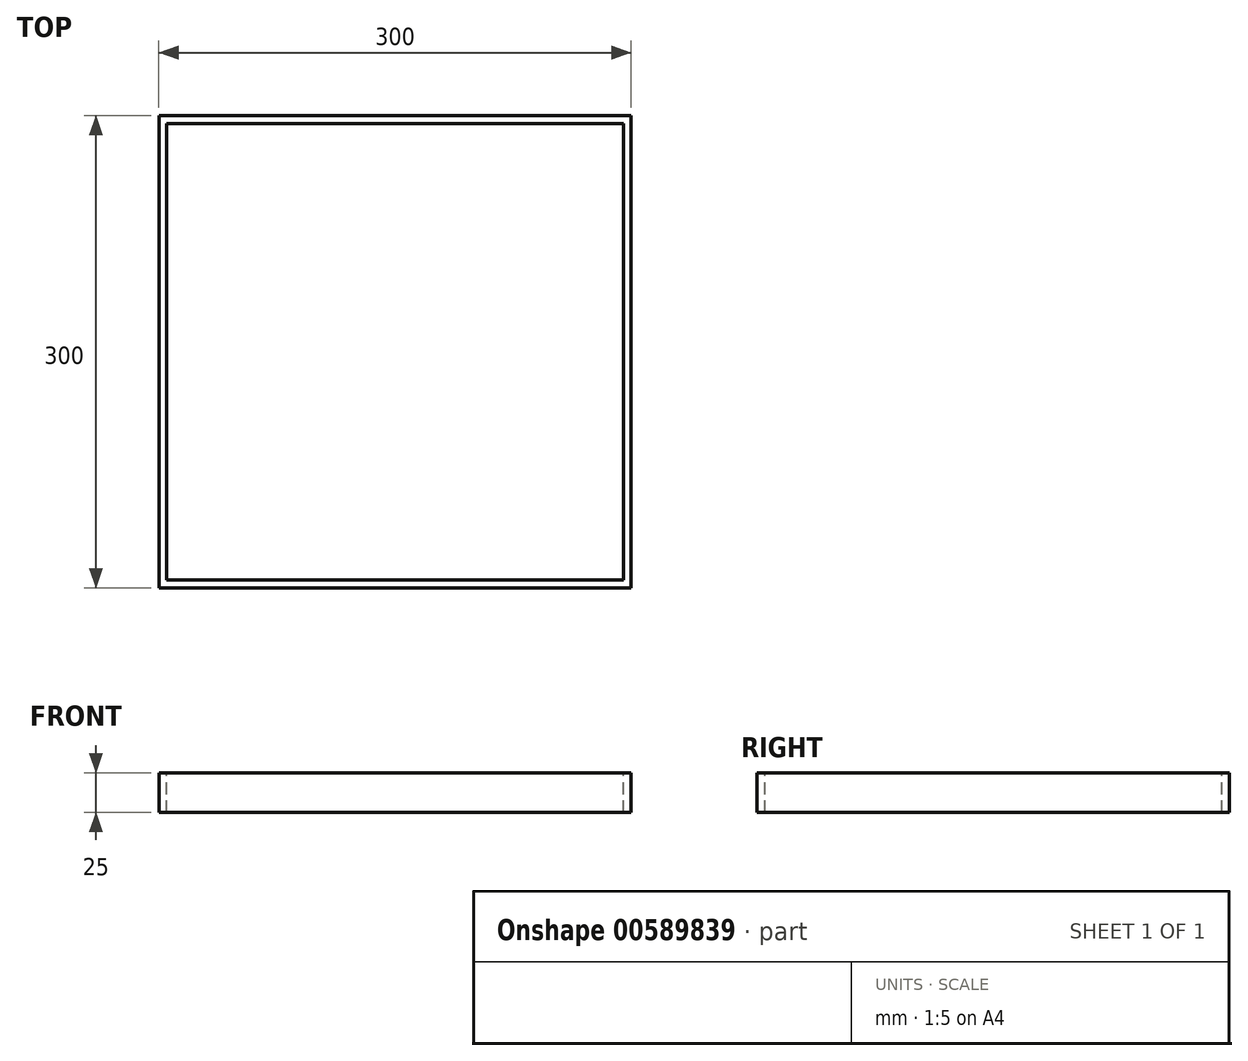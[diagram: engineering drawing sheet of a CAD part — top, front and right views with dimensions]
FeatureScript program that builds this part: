
annotation { "Feature Type Name" : "Feature", "Feature Type Description" : "" }
export const myFeature = defineFeature(function(context is Context, id is Id, definition is map)
    precondition{}
    {
        {
            var Q0;
            Q0=qCreatedBy(makeId("Top.planeOp"),FACE);
            var sketch = newSketch(context, id + "F0", { "sketchPlane" : qUnion([Q0])});
            skLineSegment(sketch, "E0.bottom", {"start": v(-140.23, 161.75) * mm, "end": v(159.77, 161.75) * mm});
            skLineSegment(sketch, "E0.top", {"start": v(-140.23, -138.25) * mm, "end": v(159.77, -138.25) * mm});
            skLineSegment(sketch, "E0.left", {"start": v(-140.23, 161.75) * mm, "end": v(-140.23, -138.25) * mm});
            skLineSegment(sketch, "E0.right", {"start": v(159.77, 161.75) * mm, "end": v(159.77, -138.25) * mm});
            skLineSegment(sketch, "E1.0", {"start": v(-135.23, 156.75) * mm, "end": v(154.77, 156.75) * mm});
            skLineSegment(sketch, "E2.0", {"start": v(-135.23, 156.75) * mm, "end": v(-135.23, -133.25) * mm});
            skLineSegment(sketch, "E3.0", {"start": v(-135.23, -133.25) * mm, "end": v(154.77, -133.25) * mm});
            skLineSegment(sketch, "E4.0", {"start": v(154.77, 156.75) * mm, "end": v(154.77, -133.25) * mm});
            skSolve(sketch);
        }
        {
            var Q0;
            Q0=sQuery(id+"F0.wireOp",EDGE,"E4.0");
            var Q1;
            Q1=sQuery(id+"F0.wireOp",EDGE,"E0.right");
            var Q2;
            Q2=sQuery(id+"F0.wireOp",EDGE,"E0.bottom");
            var Q3;
            Q3=sQuery(id+"F0.wireOp",EDGE,"E1.0");
            var Q4;
            Q4=sQuery(id+"F0.wireOp",EDGE,"E0.left");
            var Q5;
            Q5=sQuery(id+"F0.wireOp",EDGE,"E2.0");
            var Q6;
            Q6=sQuery(id+"F0.wireOp",EDGE,"E3.0");
            var Q7;
            Q7=sQuery(id+"F0.wireOp",EDGE,"E0.top");
            extrude(context, id + "F1", {"bodyType" : ToolBodyType.SURFACE, "surfaceEntities" : qUnion([Q0, Q1, Q2, Q3, Q4, Q5, Q6, Q7]), "depth" : 25 * mm, "offsetDistance" : 25 * mm});
        }
    });
